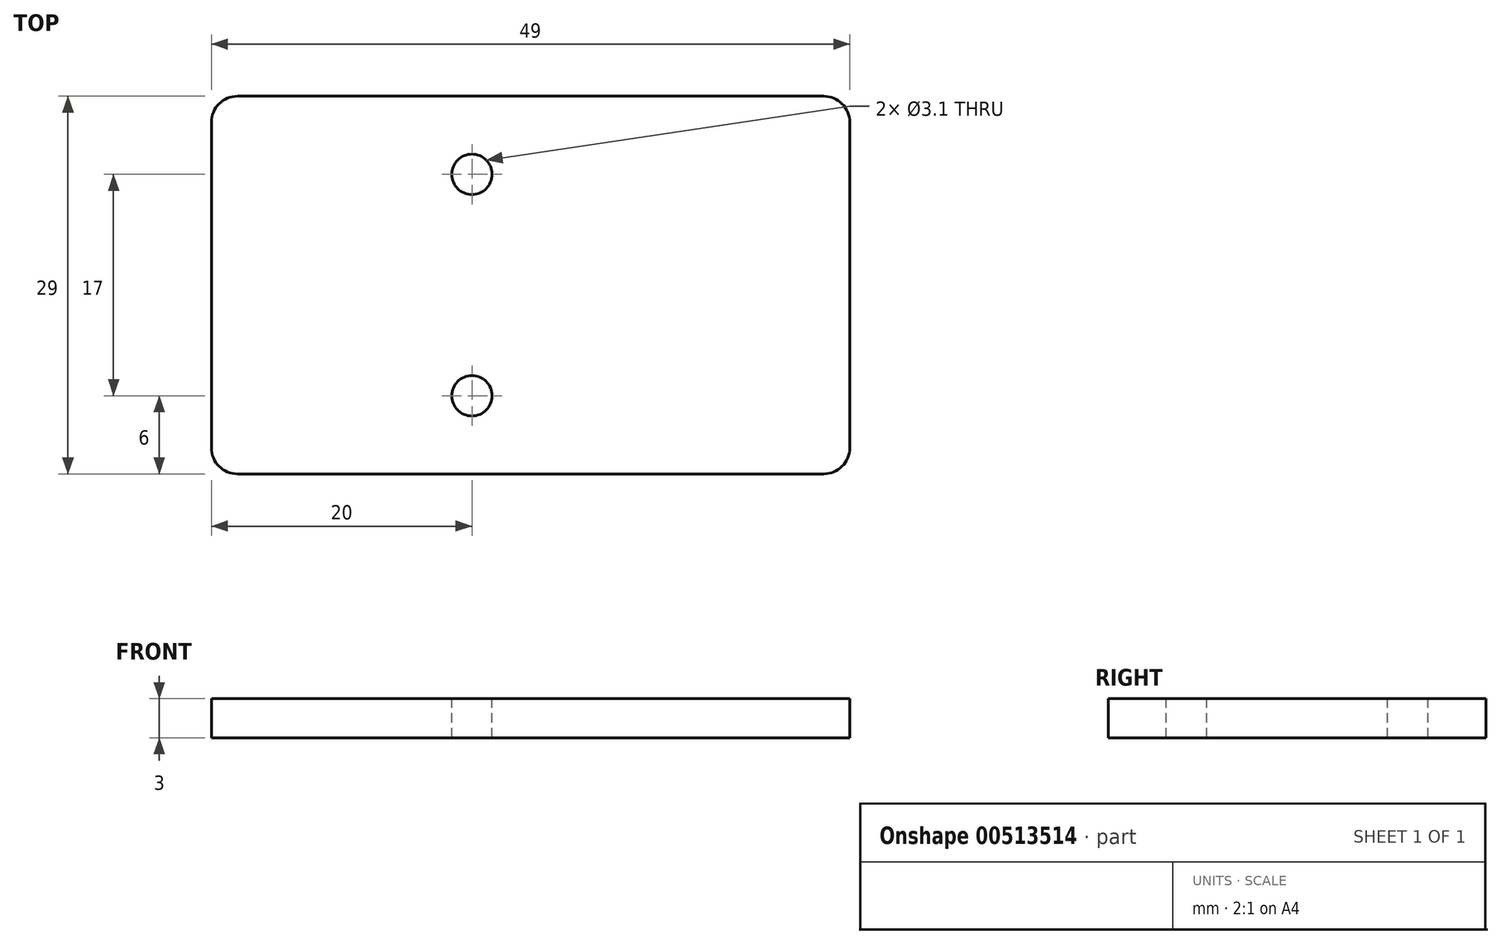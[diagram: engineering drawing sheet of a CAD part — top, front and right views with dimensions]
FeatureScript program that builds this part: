
annotation { "Feature Type Name" : "Feature", "Feature Type Description" : "" }
export const myFeature = defineFeature(function(context is Context, id is Id, definition is map)
    precondition{}
    {
        {
            var Q0;
            Q0=qCreatedBy(makeId("Top.planeOp"),FACE);
            var sketch = newSketch(context, id + "F0", { "sketchPlane" : qUnion([Q0])});
            skLineSegment(sketch, "E0.bottom", {"start": v(-24.5, 14.5) * mm, "end": v(24.5, 14.5) * mm});
            skLineSegment(sketch, "E0.top", {"start": v(-24.5, -14.5) * mm, "end": v(24.5, -14.5) * mm});
            skLineSegment(sketch, "E0.left", {"start": v(-24.5, 14.5) * mm, "end": v(-24.5, -14.5) * mm});
            skLineSegment(sketch, "E0.right", {"start": v(24.5, 14.5) * mm, "end": v(24.5, -14.5) * mm});
            skPoint(sketch, "E0.middle", {"position": v(0, 0) * mm});
            skSolve(sketch);
        }
        {
            var Q0;
            Q0 = qSketchRegion(id + "F0", true);
            extrude(context, id + "F1", {"entities" : qUnion([Q0]), "depth" : 3 * mm});
        }
        {
            var Q0;
            Q0=makeQuery(id+"F1.opExtrude","CAP_FACE",FACE,{"disambiguationData":[OSD([sQuery(id+"F0.wireOp",EDGE,"E0.bottom"),sQuery(id+"F0.wireOp",EDGE,"E0.top"),sQuery(id+"F0.wireOp",EDGE,"E0.left"),sQuery(id+"F0.wireOp",EDGE,"E0.right")])],"isStart":false});
            var sketch = newSketch(context, id + "F2", { "sketchPlane" : qUnion([Q0])});
            skCircle(sketch, "E1", {"center": v(-4.5, -8.5) * mm, "radius": 1.55 * mm});
            skCircle(sketch, "E2", {"center": v(-4.5, 8.5) * mm, "radius": 1.55 * mm});
            skSolve(sketch);
        }
        {
            var Q0;
            Q0 = qSketchRegion(id + "F2", true);
            extrude(context, id + "F3", {"entities" : qUnion([Q0]), "operationType" : NewBodyOperationType.REMOVE, "oppositeDirection" : true, "depth" : 25.4 * mm});
        }
        {
            var Q0;
            Q0=makeQuery(id+"F1.opExtrude","SWEPT_EDGE",EDGE,{"disambiguationData":[OSD([sQuery(id+"F0.wireOp",EDGE,"E0.bottom"),sQuery(id+"F0.wireOp",EDGE,"E0.left")])]});
            var Q1;
            Q1=makeQuery(id+"F1.opExtrude","SWEPT_EDGE",EDGE,{"disambiguationData":[OSD([sQuery(id+"F0.wireOp",EDGE,"E0.top"),sQuery(id+"F0.wireOp",EDGE,"E0.left")])]});
            var Q2;
            Q2=makeQuery(id+"F1.opExtrude","SWEPT_EDGE",EDGE,{"disambiguationData":[OSD([sQuery(id+"F0.wireOp",EDGE,"E0.top"),sQuery(id+"F0.wireOp",EDGE,"E0.right")])]});
            var Q3;
            Q3=makeQuery(id+"F1.opExtrude","SWEPT_EDGE",EDGE,{"disambiguationData":[OSD([sQuery(id+"F0.wireOp",EDGE,"E0.bottom"),sQuery(id+"F0.wireOp",EDGE,"E0.right")])]});
            fillet(context, id + "F4", {"entities" : qUnion([Q0, Q1, Q2, Q3]), "radius" : 2 * mm, "tangentPropagation" : true, "allowEdgeOverflow" : false});
        }
    });
